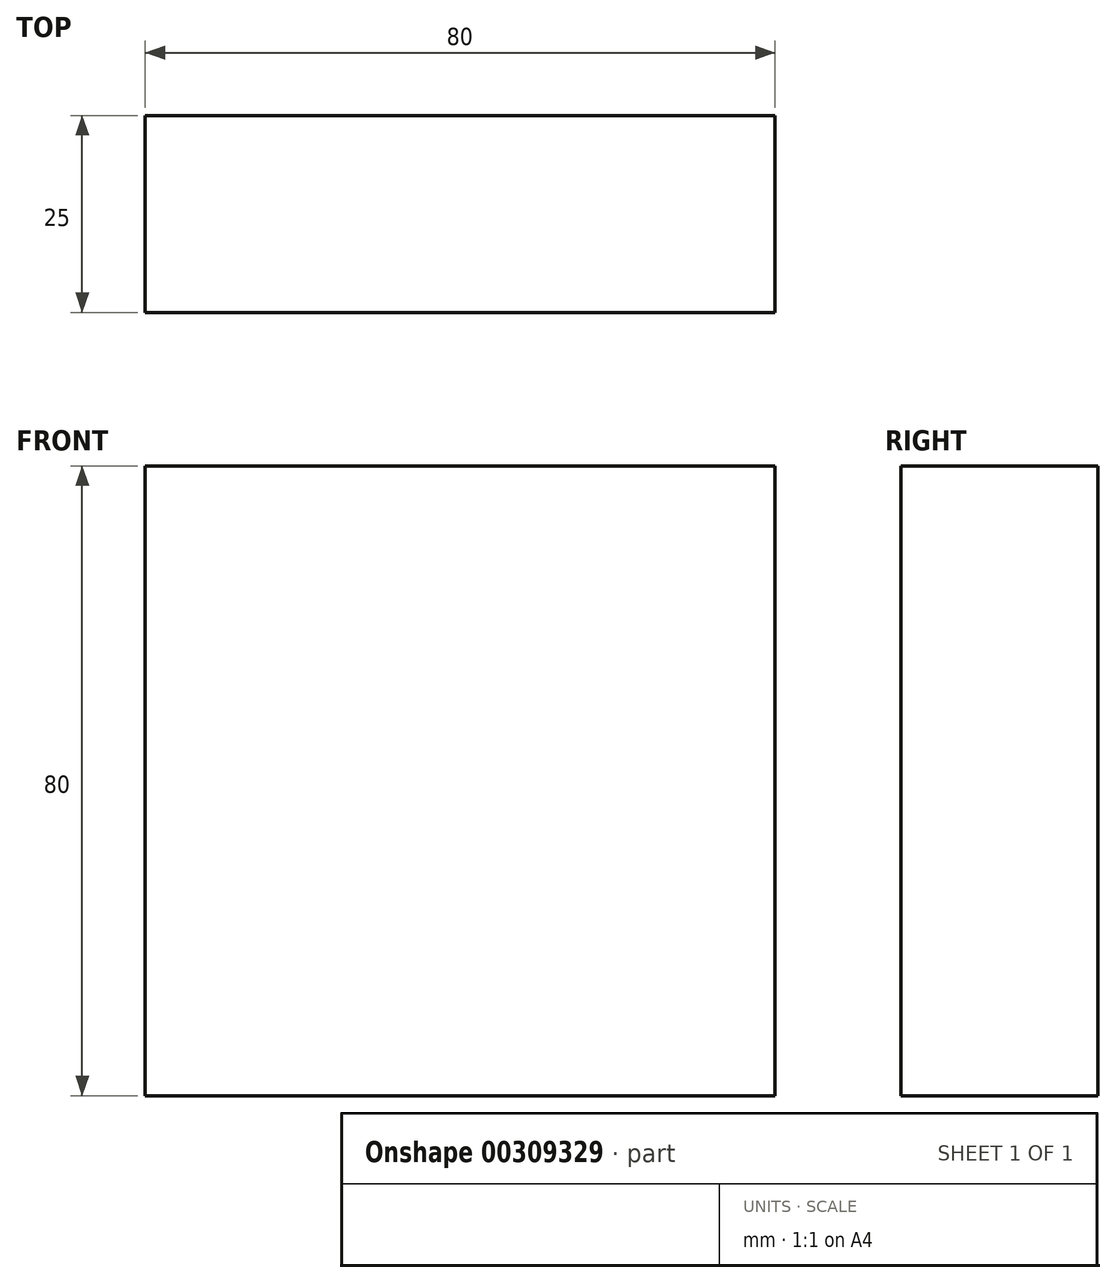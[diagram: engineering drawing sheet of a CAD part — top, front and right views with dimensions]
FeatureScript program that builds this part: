
annotation { "Feature Type Name" : "Feature", "Feature Type Description" : "" }
export const myFeature = defineFeature(function(context is Context, id is Id, definition is map)
    precondition{}
    {
        {
            var Q0;
            Q0=qCreatedBy(makeId("Front.planeOp"),FACE);
            var sketch = newSketch(context, id + "F0", { "sketchPlane" : qUnion([Q0])});
            skLineSegment(sketch, "E0.bottom", {"start": v(40, 40) * mm, "end": v(-40, 40) * mm});
            skLineSegment(sketch, "E0.top", {"start": v(40, -40) * mm, "end": v(-40, -40) * mm});
            skLineSegment(sketch, "E0.left", {"start": v(40, 40) * mm, "end": v(40, -40) * mm});
            skLineSegment(sketch, "E0.right", {"start": v(-40, 40) * mm, "end": v(-40, -40) * mm});
            skPoint(sketch, "E0.middle", {"position": v(0, 0) * mm});
            skSolve(sketch);
        }
        {
            var Q0;
            Q0 = qSketchRegion(id + "F0", true);
            extrude(context, id + "F1", {"entities" : qUnion([Q0]), "depth" : 25 * mm});
        }
    });
